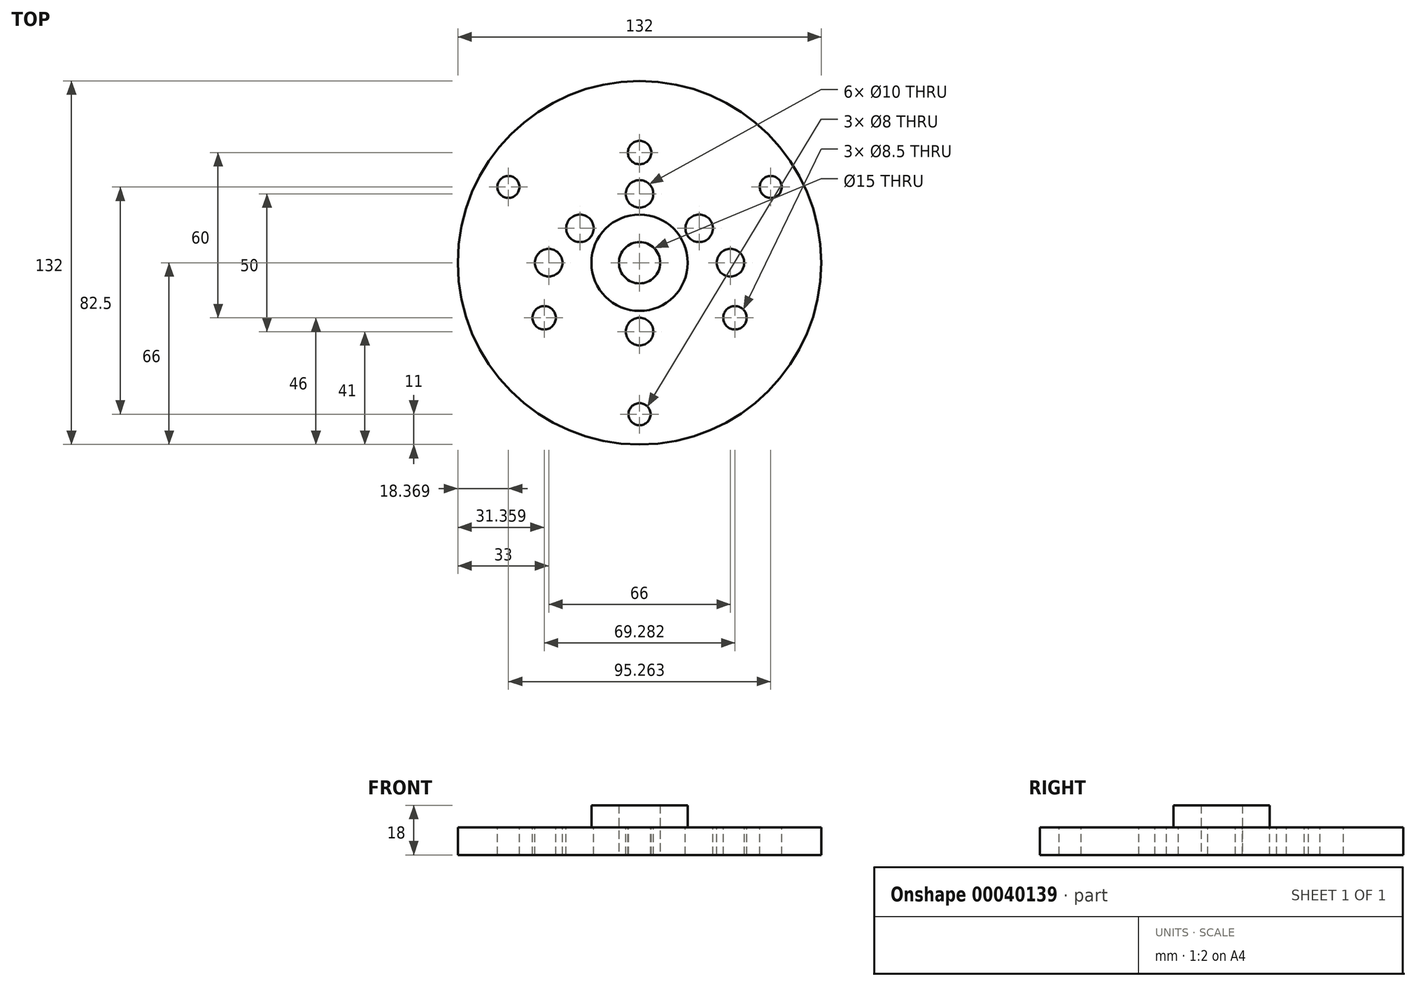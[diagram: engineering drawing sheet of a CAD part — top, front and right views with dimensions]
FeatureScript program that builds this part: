
annotation { "Feature Type Name" : "Feature", "Feature Type Description" : "" }
export const myFeature = defineFeature(function(context is Context, id is Id, definition is map)
    precondition{}
    {
        {
            var Q0;
            Q0=qCreatedBy(makeId("Top.planeOp"),FACE);
            var sketch = newSketch(context, id + "F0", { "sketchPlane" : qUnion([Q0])});
            skCircle(sketch, "E0", {"center": v(0, 0) * mm, "radius": 66 * mm});
            skCircle(sketch, "E1", {"center": v(0, 0) * mm, "radius": 7.5 * mm});
            skCircle(sketch, "E2", {"center": v(0, 0) * mm, "radius": 17.5 * mm});
            skSolve(sketch);
        }
        {
            var Q0;
            Q0=makeQuery(id+"F0.imprint","IMPRINT",FACE,{"disambiguationData":[TD([[makeQuery(id+"F0.imprint","IMPRINT",EDGE,{"derivedFrom":sQuery(id+"F0.wireOp",EDGE,"E0")}),1.0]])]});
            var Q1;
            Q1=makeQuery(id+"F0.imprint","IMPRINT",FACE,{"disambiguationData":[TD([[makeQuery(id+"F0.imprint","IMPRINT",EDGE,{"derivedFrom":sQuery(id+"F0.wireOp",EDGE,"E1")}),-1.0]])]});
            var Q2;
            Q2=sQuery(id+"F0.wireOp",EDGE,"E0");
            extrude(context, id + "F1", {"entities" : qUnion([Q0, Q1]), "surfaceEntities" : qUnion([Q2]), "depth" : 10 * mm});
        }
        {
            var Q0;
            Q0=makeQuery(id+"F0.imprint","IMPRINT",FACE,{"disambiguationData":[TD([[makeQuery(id+"F0.imprint","IMPRINT",EDGE,{"derivedFrom":sQuery(id+"F0.wireOp",EDGE,"E1")}),-1.0]])]});
            extrude(context, id + "F2", {"entities" : qUnion([Q0]), "operationType" : NewBodyOperationType.ADD, "depth" : 18 * mm});
        }
        {
            var Q0;
            Q0=makeQuery(id+"F1.opExtrude","CAP_FACE",FACE,{"disambiguationData":[OSD([sQuery(id+"F0.wireOp",EDGE,"E0"),sQuery(id+"F0.wireOp",EDGE,"E1")])],"isStart":false});
            var sketch = newSketch(context, id + "F3", { "sketchPlane" : qUnion([Q0])});
            skCircle(sketch, "E3", {"center": v(0, 0) * mm, "radius": 25 * mm, "construction": true});
            skCircle(sketch, "E4", {"center": v(0, 0) * mm, "radius": 33 * mm, "construction": true});
            skCircle(sketch, "E5", {"center": v(0, 0) * mm, "radius": 40 * mm, "construction": true});
            skCircle(sketch, "E6", {"center": v(0, 0) * mm, "radius": 55 * mm, "construction": true});
            skLineSegment(sketch, "E7", {"start": v(-66, 0) * mm, "end": v(66, 0) * mm, "construction": true});
            skLineSegment(sketch, "E8", {"start": v(-57.16, 33) * mm, "end": v(57.16, -33) * mm, "construction": true});
            skLineSegment(sketch, "E9", {"start": v(-57.16, -33) * mm, "end": v(57.16, 33) * mm, "construction": true});
            skLineSegment(sketch, "E10", {"start": v(0, -66) * mm, "end": v(0, 66) * mm, "construction": true});
            skCircle(sketch, "E11", {"center": v(0, -25) * mm, "radius": 5 * mm});
            skCircle(sketch, "E12", {"center": v(21.65, 12.5) * mm, "radius": 5 * mm});
            skCircle(sketch, "E13", {"center": v(0, 25) * mm, "radius": 5 * mm});
            skCircle(sketch, "E14", {"center": v(-21.65, 12.5) * mm, "radius": 5 * mm});
            skCircle(sketch, "E15", {"center": v(-33, 0) * mm, "radius": 5 * mm});
            skCircle(sketch, "E16", {"center": v(33, 0) * mm, "radius": 5 * mm});
            skCircle(sketch, "E17", {"center": v(-34.64, -20) * mm, "radius": 4.25 * mm});
            skCircle(sketch, "E18", {"center": v(0, 40) * mm, "radius": 4.25 * mm});
            skCircle(sketch, "E19", {"center": v(34.64, -20) * mm, "radius": 4.25 * mm});
            skCircle(sketch, "E20", {"center": v(0, -55) * mm, "radius": 4 * mm});
            skCircle(sketch, "E21", {"center": v(-47.63, 27.5) * mm, "radius": 4 * mm});
            skCircle(sketch, "E22", {"center": v(47.63, 27.5) * mm, "radius": 4 * mm});
            skSolve(sketch);
        }
        {
            var Q0;
            Q0 = qSketchRegion(id + "F3", true);
            extrude(context, id + "F4", {"entities" : qUnion([Q0]), "operationType" : NewBodyOperationType.REMOVE, "endBound" : BoundingType.UP_TO_NEXT, "oppositeDirection" : true, "depth" : 25 * mm});
        }
    });
